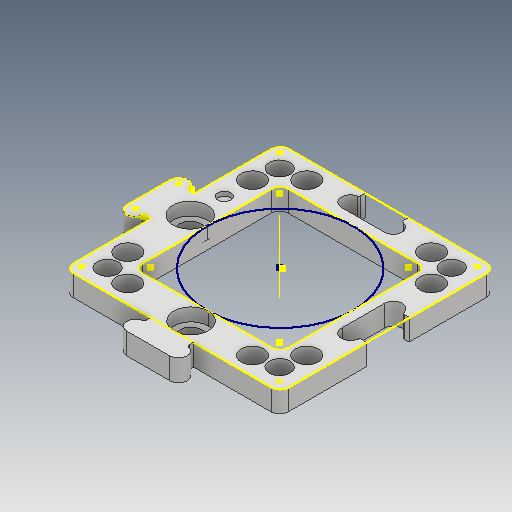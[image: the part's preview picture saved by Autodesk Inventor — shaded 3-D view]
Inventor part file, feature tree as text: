
AUTODESK INVENTOR PART (.ipt)
format: ipt  version: 2019.4 (Build 234330000, 330)  size: 509,952 bytes
history: native  units: mm
features: sketch x7, projected_geometry x6, extrude x5, mirror x2, pattern_circular x2, other x1, hole x1
ambient origin geometry x8: Origin, YZ Plane, XZ Plane, XY Plane, X Axis, Y Axis, Z Axis, Center Point
bodies: Volumenkörper1 (feature_tree)
feature tree (24):
  extrude  "Extrusion1"  TaperAngle=0.0deg  [1 undecoded]
  mirror  "Mirror6"
  mirror  "Mirror7"
  extrude  "Extrusion13"  TaperAngle=0.0deg  [1 undecoded]
  sketch  "Sketch27"  dims[d9=0.0mm d13=0.0mm]
  extrude  "Extrusion14"  TaperAngle=0.0deg  [1 undecoded]
  other  "Work Axis4"
  pattern_circular  "Circular Pattern6"  [2 undecoded]
  hole  "Hole7"  [1 undecoded]
  extrude  "Extrusion15"  Depth=3.0mm
  pattern_circular  "Circular Pattern7"  [2 undecoded]
  extrude  "Extrusion16"  TaperAngle=0.0deg  [1 undecoded]
  sketch  "Skizze1"  dims[d5=0.0mm d6=0.0mm]
  sketch  "Sketch26"  dims[d7=0.0mm d8=0.0mm]
  projected_geometry  "Projected Loop21"
  projected_geometry  "Projected Loop22"
  sketch  "Sketch28"  dims[d14=0.0mm]
  projected_geometry  "Projected Loop23"
  sketch  "Sketch29"  dims[d20=0.0mm]
  projected_geometry  "Projected Loop24"
  sketch  "Sketch30"  dims[d21=0.0mm]
  projected_geometry  "Projected Loop25"
  sketch  "Sketch31"  dims[d22=0.0mm d23=0.0mm d24=0.0mm d25=3.0mm d26=0.0mm d27=0.0mm d28=0.0mm d29=0.0mm d30=0.0mm d31=0.0mm d32=0.0mm d33=0.0mm d34=0.0mm d46=0.0mm d47=0.0mm d48=0.0mm d49=-10.0mm d50=0.0mm d51=0.0mm d52=0.0mm d53=0.0mm d54=0.0mm d55=0.0mm d56=0.0mm d57=0.0mm d58=0.0mm d59=0.0mm d77=2.65mm d82=2.65mm d222=0.5mm d236=5.3mm d278=25.0mm d279=25.0mm d2=8.0mm d281=8.0mm d282=2.0mm d283=4.85mm d284=20.0mm d4=20.0mm d286=5.3mm d290=20.8mm d292=2.0mm d293=5.5mm d294=14.0mm d295=18.0mm d296=10.0mm d297=1.5mm d298=10.0mm d299=0.0mm d300=2.0mm d301=0.5mm d302=10.0mm d303=0.0mm d307=0.075mm d308=20.0mm d309=90.0deg d313=6.3mm d314=6.3mm d315=0.194632mm d316=0.0mm d317=0.0mm d318=0.090102mm d319=7.78mm d320=4.0mm d321=21.4mm d322=4.0mm d323=5.0mm d324=6.0mm d325=8.0mm d326=3.0mm d327=90.0deg d328=8.0mm d329=20.594885mm d330=0.0mm d331=0.0mm d332=0.0mm d334=14.0mm d336=10.0mm d337=1.5mm d338=2.0mm d339=0.5mm d340=0.075mm d341=0.075mm d342=0.075mm d343=0.075mm d344=10.0mm d345=0.0mm d346=0.075mm d347=0.0mm d348=20.0mm d349=90.0deg d351=3.0mm d352=1.0mm d353=0.0mm]
  projected_geometry  "Projected Loop26"
note: 9 required parameter values undecoded (feature->parameter linkage not recoverable at this tier; creation-order binding heuristic only, values carry confidence <= 0.55)
